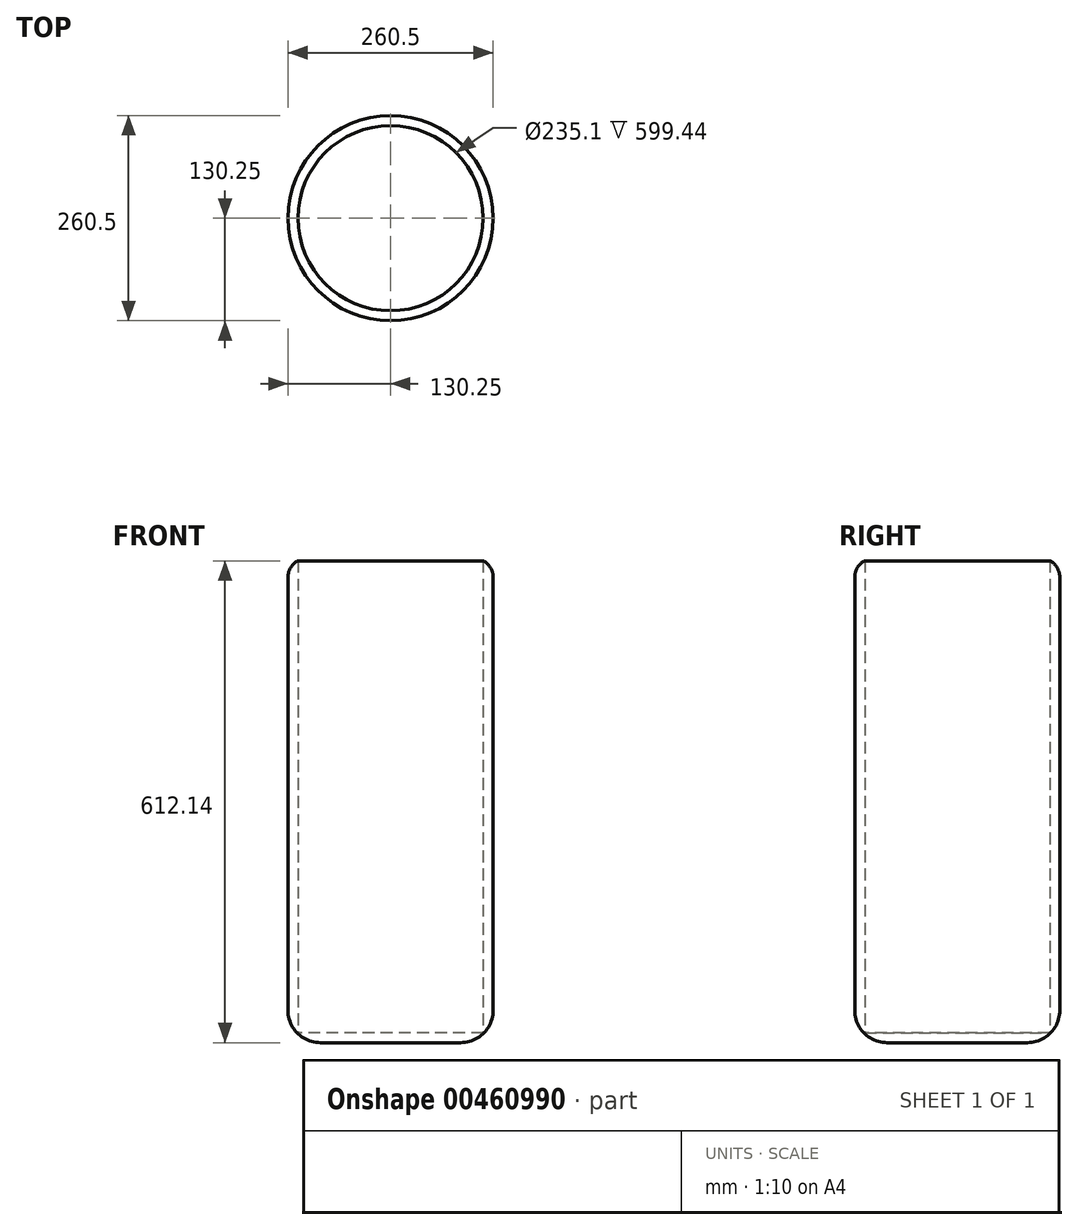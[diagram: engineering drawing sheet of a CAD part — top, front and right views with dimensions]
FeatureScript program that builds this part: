
annotation { "Feature Type Name" : "Feature", "Feature Type Description" : "" }
export const myFeature = defineFeature(function(context is Context, id is Id, definition is map)
    precondition{}
    {
        {
            var Q0;
            Q0=qCreatedBy(makeId("Top.planeOp"),FACE);
            var sketch = newSketch(context, id + "F0", { "sketchPlane" : qUnion([Q0])});
            skCircle(sketch, "E0", {"center": v(0, 0) * mm, "radius": 117.55 * mm});
            skSolve(sketch);
        }
        {
            var Q0;
            Q0 = qSketchRegion(id + "F0", true);
            extrude(context, id + "F1", {"entities" : qUnion([Q0]), "depth" : 599.44 * mm});
        }
        {
            var Q0;
            Q0=makeQuery(id+"F1.opExtrude","CAP_FACE",FACE,{"disambiguationData":[OSD([sQuery(id+"F0.wireOp",EDGE,"E0")])],"isStart":false});
            shell(context, id + "F2", {"entities" : qUnion([Q0]), "thickness" : 12.7 * mm, "oppositeDirection" : true});
        }
        {
            var Q0;
            Q0=makeQuery(id+"F1.opExtrude","CAP_EDGE",EDGE,{"disambiguationData":[OSD([sQuery(id+"F0.wireOp",EDGE,"E0")])],"isStart":false});
            fillet(context, id + "F3", {"entities" : qUnion([Q0]), "radius" : 23.3 * mm, "tangentPropagation" : true, "allowEdgeOverflow" : false});
        }
        {
            var Q0;
            Q0=makeQuery(id+"F1.opExtrude","CAP_EDGE",EDGE,{"disambiguationData":[OSD([sQuery(id+"F0.wireOp",EDGE,"E0")])],"isStart":true});
            fillet(context, id + "F4", {"entities" : qUnion([Q0]), "radius" : 41.1 * mm, "tangentPropagation" : true, "allowEdgeOverflow" : false});
        }
    });
